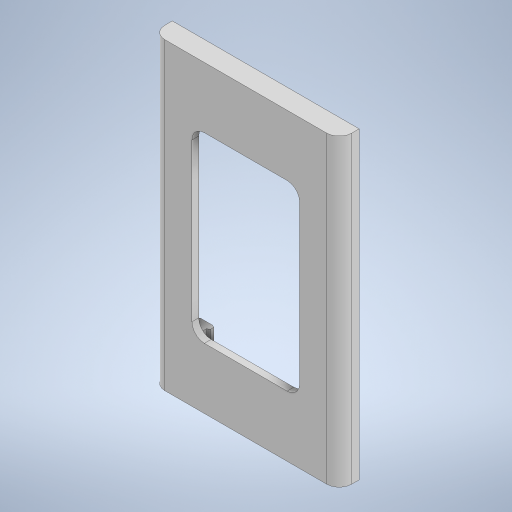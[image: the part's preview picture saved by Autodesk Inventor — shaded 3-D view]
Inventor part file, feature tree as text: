
AUTODESK INVENTOR PART (.ipt)
format: ipt  version: 2023 (Build 270158000, 158)  size: 343,040 bytes
history: native  units: mm
features: sketch x5, extrude x4, other x2, fillet x2, chamfer x2, mirror x2, shell x1
ambient origin geometry x8: Origin, YZ Plane, XZ Plane, XY Plane, X Axis, Y Axis, Z Axis, Center Point
bodies: Body1 (feature_tree)
feature tree (18):
  other  "솔리드1"
  extrude  "돌출1"  Depth=75.0mm
  fillet  "모깎기1"  Radius=122.0mm
  shell  "쉘1"  Thickness=43.2mm
  extrude  "돌출2"  Depth=73.2mm
  extrude  "돌출3"  Depth=8.0mm TaperAngle=0.0deg
  chamfer  "모따기1"  Distance=5.0mm
  extrude  "돌출4"  Depth=1.7mm
  mirror  "미러1"
  mirror  "미러2"
  sketch  "스케치5"
  fillet  "모깎기6"  Radius=8.0mm
  chamfer  "모따기2"  Distance=36.85mm
  other  "두껍게 하기1"
  sketch  "스케치1"
  sketch  "스케치2"
  sketch  "스케치3"
  sketch  "스케치4"
